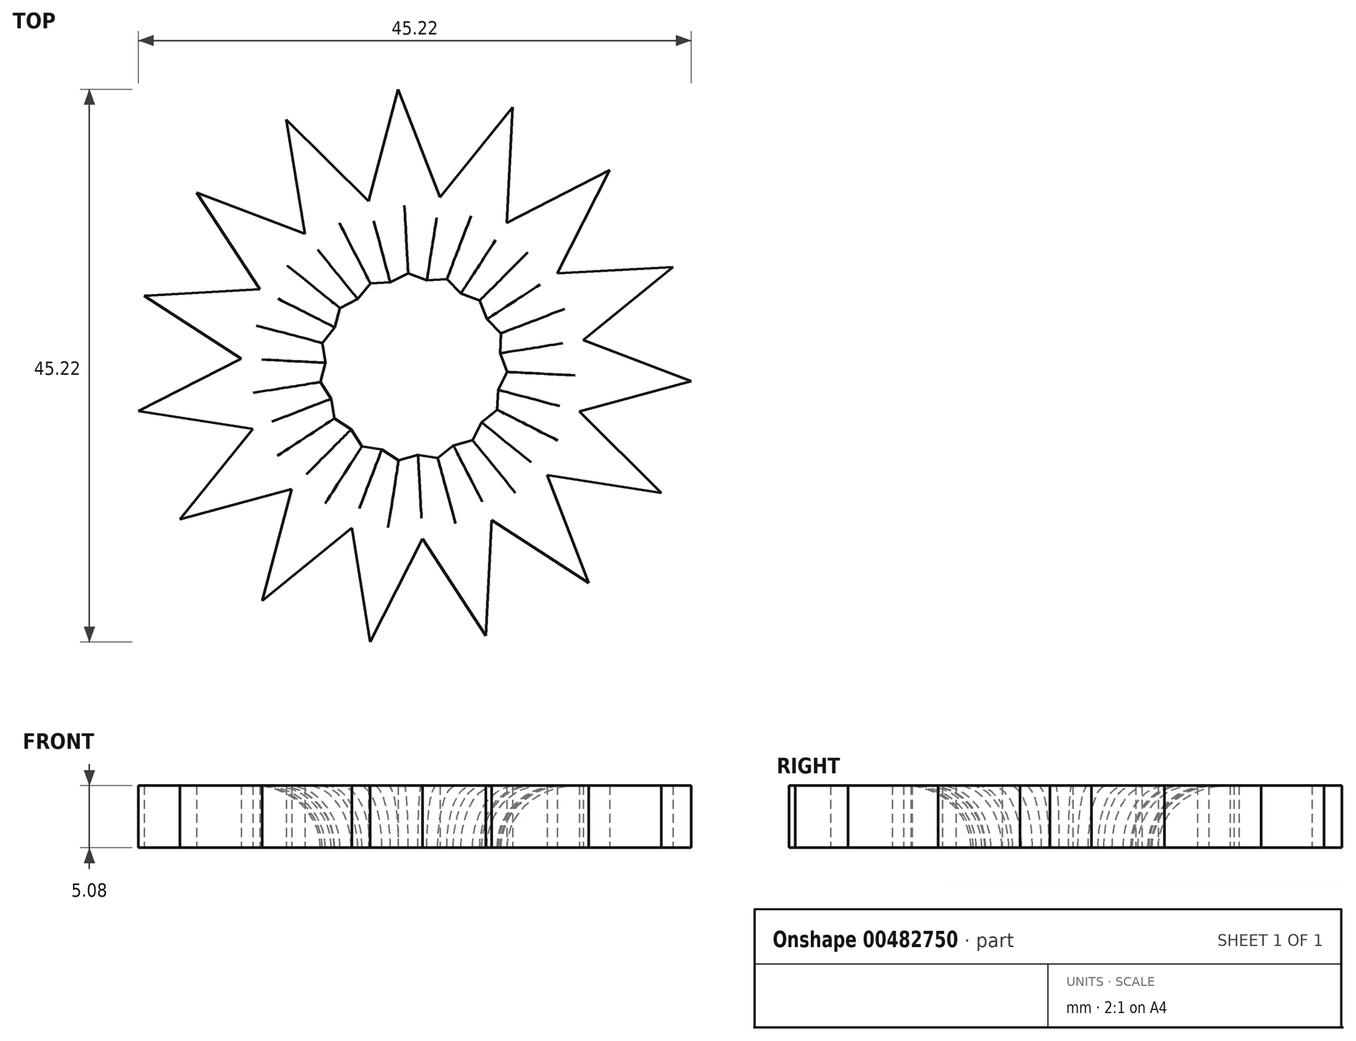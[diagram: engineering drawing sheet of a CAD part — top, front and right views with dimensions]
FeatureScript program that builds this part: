
annotation { "Feature Type Name" : "Feature", "Feature Type Description" : "" }
export const myFeature = defineFeature(function(context is Context, id is Id, definition is map)
    precondition{}
    {
        {
            var Q0;
            Q0=qCreatedBy(makeId("Top.planeOp"),FACE);
            var sketch = newSketch(context, id + "F0", { "sketchPlane" : qUnion([Q0])});
            skLineSegment(sketch, "E0", {"start": v(-12.36, -19.11) * mm, "end": v(-1.23, 22.73) * mm});
            skLineSegment(sketch, "E1", {"start": v(-1.23, 22.73) * mm, "end": v(14.36, -17.67) * mm});
            skLineSegment(sketch, "E2", {"start": v(14.36, -17.67) * mm, "end": v(-22, 5.85) * mm});
            skLineSegment(sketch, "E3", {"start": v(-22, 5.85) * mm, "end": v(21.24, 8.2) * mm});
            skLineSegment(sketch, "E4", {"start": v(21.24, 8.2) * mm, "end": v(-12.36, -19.11) * mm});
            skLineSegment(sketch, "E5", {"start": v(-19.07, -12.43) * mm, "end": v(8.12, 21.27) * mm});
            skLineSegment(sketch, "E6", {"start": v(8.12, 21.27) * mm, "end": v(5.93, -21.98) * mm});
            skLineSegment(sketch, "E7", {"start": v(5.93, -21.98) * mm, "end": v(-17.72, 14.3) * mm});
            skLineSegment(sketch, "E8", {"start": v(-17.72, 14.3) * mm, "end": v(22.74, -1.15) * mm});
            skLineSegment(sketch, "E9", {"start": v(22.74, -1.15) * mm, "end": v(-19.07, -12.43) * mm});
            skLineSegment(sketch, "E10", {"start": v(-3.52, -22.5) * mm, "end": v(-10.37, 20.26) * mm});
            skLineSegment(sketch, "E11", {"start": v(-10.37, 20.26) * mm, "end": v(20.3, -10.3) * mm});
            skLineSegment(sketch, "E12", {"start": v(20.3, -10.3) * mm, "end": v(-22.48, -3.6) * mm});
            skLineSegment(sketch, "E13", {"start": v(-22.48, -3.6) * mm, "end": v(16.07, 16.13) * mm});
            skLineSegment(sketch, "E14", {"start": v(16.07, 16.13) * mm, "end": v(-3.52, -22.5) * mm});
            skSolve(sketch);
        }
        {
            var Q0;
            {var subQ0=sQuery(id+"F0.wireOp",EDGE,"E3");var subQ1=sQuery(id+"F0.wireOp",EDGE,"E2");var subQ2=makeQuery(id+"F0.imprint","INTERSECT",VERTEX,{"derivedFrom":[subQ1,subQ0]});Q0=makeQuery(id+"F0.imprint","IMPRINT",FACE,{"disambiguationData":[TD([[makeQuery(id+"F0.imprint","IMPRINT",EDGE,{"disambiguationData":[TD([[subQ2,1.0]])],"derivedFrom":subQ1}),-1.0]])]});}
            var Q1;
            {var subQ0=sQuery(id+"F0.wireOp",EDGE,"E13");var subQ1=sQuery(id+"F0.wireOp",EDGE,"E2");var subQ2=makeQuery(id+"F0.imprint","INTERSECT",VERTEX,{"derivedFrom":[subQ1,subQ0]});Q1=makeQuery(id+"F0.imprint","IMPRINT",FACE,{"disambiguationData":[TD([[makeQuery(id+"F0.imprint","IMPRINT",EDGE,{"disambiguationData":[TD([[subQ2,1.0]])],"derivedFrom":subQ1}),1.0]])]});}
            var Q2;
            {var subQ0=sQuery(id+"F0.wireOp",EDGE,"E9");var subQ1=sQuery(id+"F0.wireOp",EDGE,"E0");var subQ2=makeQuery(id+"F0.imprint","INTERSECT",VERTEX,{"derivedFrom":[subQ1,subQ0]});Q2=makeQuery(id+"F0.imprint","IMPRINT",FACE,{"disambiguationData":[TD([[makeQuery(id+"F0.imprint","IMPRINT",EDGE,{"disambiguationData":[TD([[subQ2,-1.0]])],"derivedFrom":subQ1}),1.0]])]});}
            var Q3;
            {var subQ0=sQuery(id+"F0.wireOp",EDGE,"E4");var subQ1=sQuery(id+"F0.wireOp",EDGE,"E0");var subQ2=makeQuery(id+"F0.imprint","INTERSECT",VERTEX,{"derivedFrom":[subQ1,subQ0]});Q3=makeQuery(id+"F0.imprint","IMPRINT",FACE,{"disambiguationData":[TD([[makeQuery(id+"F0.imprint","IMPRINT",EDGE,{"disambiguationData":[TD([[subQ2,-1.0]])],"derivedFrom":subQ1}),-1.0]])]});}
            var Q4;
            {var subQ0=sQuery(id+"F0.wireOp",EDGE,"E10");var subQ1=sQuery(id+"F0.wireOp",EDGE,"E4");var subQ2=makeQuery(id+"F0.imprint","INTERSECT",VERTEX,{"derivedFrom":[subQ1,subQ0]});Q4=makeQuery(id+"F0.imprint","IMPRINT",FACE,{"disambiguationData":[TD([[makeQuery(id+"F0.imprint","IMPRINT",EDGE,{"disambiguationData":[TD([[subQ2,1.0]])],"derivedFrom":subQ1}),1.0]])]});}
            var Q5;
            {var subQ0=sQuery(id+"F0.wireOp",EDGE,"E6");var subQ1=sQuery(id+"F0.wireOp",EDGE,"E2");var subQ2=makeQuery(id+"F0.imprint","INTERSECT",VERTEX,{"derivedFrom":[subQ1,subQ0]});Q5=makeQuery(id+"F0.imprint","IMPRINT",FACE,{"disambiguationData":[TD([[makeQuery(id+"F0.imprint","IMPRINT",EDGE,{"disambiguationData":[TD([[subQ2,-1.0]])],"derivedFrom":subQ1}),1.0]])]});}
            var Q6;
            {var subQ0=sQuery(id+"F0.wireOp",EDGE,"E2");var subQ1=sQuery(id+"F0.wireOp",EDGE,"E1");var subQ2=makeQuery(id+"F0.imprint","INTERSECT",VERTEX,{"derivedFrom":[subQ1,subQ0]});Q6=makeQuery(id+"F0.imprint","IMPRINT",FACE,{"disambiguationData":[TD([[makeQuery(id+"F0.imprint","IMPRINT",EDGE,{"disambiguationData":[TD([[subQ2,1.0]])],"derivedFrom":subQ1}),-1.0]])]});}
            var Q7;
            {var subQ0=sQuery(id+"F0.wireOp",EDGE,"E12");var subQ1=sQuery(id+"F0.wireOp",EDGE,"E1");var subQ2=makeQuery(id+"F0.imprint","INTERSECT",VERTEX,{"derivedFrom":[subQ1,subQ0]});Q7=makeQuery(id+"F0.imprint","IMPRINT",FACE,{"disambiguationData":[TD([[makeQuery(id+"F0.imprint","IMPRINT",EDGE,{"disambiguationData":[TD([[subQ2,1.0]])],"derivedFrom":subQ1}),1.0]])]});}
            var Q8;
            {var subQ0=sQuery(id+"F0.wireOp",EDGE,"E8");var subQ1=sQuery(id+"F0.wireOp",EDGE,"E4");var subQ2=makeQuery(id+"F0.imprint","INTERSECT",VERTEX,{"derivedFrom":[subQ1,subQ0]});Q8=makeQuery(id+"F0.imprint","IMPRINT",FACE,{"disambiguationData":[TD([[makeQuery(id+"F0.imprint","IMPRINT",EDGE,{"disambiguationData":[TD([[subQ2,-1.0]])],"derivedFrom":subQ1}),1.0]])]});}
            var Q9;
            {var subQ0=sQuery(id+"F0.wireOp",EDGE,"E4");var subQ1=sQuery(id+"F0.wireOp",EDGE,"E3");var subQ2=makeQuery(id+"F0.imprint","INTERSECT",VERTEX,{"derivedFrom":[subQ1,subQ0]});Q9=makeQuery(id+"F0.imprint","IMPRINT",FACE,{"disambiguationData":[TD([[makeQuery(id+"F0.imprint","IMPRINT",EDGE,{"disambiguationData":[TD([[subQ2,1.0]])],"derivedFrom":subQ1}),-1.0]])]});}
            var Q10;
            {var subQ0=sQuery(id+"F0.wireOp",EDGE,"E14");var subQ1=sQuery(id+"F0.wireOp",EDGE,"E3");var subQ2=makeQuery(id+"F0.imprint","INTERSECT",VERTEX,{"derivedFrom":[subQ1,subQ0]});Q10=makeQuery(id+"F0.imprint","IMPRINT",FACE,{"disambiguationData":[TD([[makeQuery(id+"F0.imprint","IMPRINT",EDGE,{"disambiguationData":[TD([[subQ2,1.0]])],"derivedFrom":subQ1}),1.0]])]});}
            var Q11;
            {var subQ0=sQuery(id+"F0.wireOp",EDGE,"E5");var subQ1=sQuery(id+"F0.wireOp",EDGE,"E1");var subQ2=makeQuery(id+"F0.imprint","INTERSECT",VERTEX,{"derivedFrom":[subQ1,subQ0]});Q11=makeQuery(id+"F0.imprint","IMPRINT",FACE,{"disambiguationData":[TD([[makeQuery(id+"F0.imprint","IMPRINT",EDGE,{"disambiguationData":[TD([[subQ2,-1.0]])],"derivedFrom":subQ1}),1.0]])]});}
            var Q12;
            {var subQ0=sQuery(id+"F0.wireOp",EDGE,"E1");var subQ1=sQuery(id+"F0.wireOp",EDGE,"E0");var subQ2=makeQuery(id+"F0.imprint","INTERSECT",VERTEX,{"derivedFrom":[subQ1,subQ0]});Q12=makeQuery(id+"F0.imprint","IMPRINT",FACE,{"disambiguationData":[TD([[makeQuery(id+"F0.imprint","IMPRINT",EDGE,{"disambiguationData":[TD([[subQ2,1.0]])],"derivedFrom":subQ1}),-1.0]])]});}
            var Q13;
            {var subQ0=sQuery(id+"F0.wireOp",EDGE,"E11");var subQ1=sQuery(id+"F0.wireOp",EDGE,"E0");var subQ2=makeQuery(id+"F0.imprint","INTERSECT",VERTEX,{"derivedFrom":[subQ1,subQ0]});Q13=makeQuery(id+"F0.imprint","IMPRINT",FACE,{"disambiguationData":[TD([[makeQuery(id+"F0.imprint","IMPRINT",EDGE,{"disambiguationData":[TD([[subQ2,1.0]])],"derivedFrom":subQ1}),1.0]])]});}
            var Q14;
            {var subQ0=sQuery(id+"F0.wireOp",EDGE,"E7");var subQ1=sQuery(id+"F0.wireOp",EDGE,"E3");var subQ2=makeQuery(id+"F0.imprint","INTERSECT",VERTEX,{"derivedFrom":[subQ1,subQ0]});Q14=makeQuery(id+"F0.imprint","IMPRINT",FACE,{"disambiguationData":[TD([[makeQuery(id+"F0.imprint","IMPRINT",EDGE,{"disambiguationData":[TD([[subQ2,-1.0]])],"derivedFrom":subQ1}),1.0]])]});}
            var Q15;
            {var subQ0=sQuery(id+"F0.wireOp",EDGE,"E7");var subQ1=sQuery(id+"F0.wireOp",EDGE,"E3");var subQ2=makeQuery(id+"F0.imprint","INTERSECT",VERTEX,{"derivedFrom":[subQ1,subQ0]});Q15=makeQuery(id+"F0.imprint","IMPRINT",FACE,{"disambiguationData":[TD([[makeQuery(id+"F0.imprint","IMPRINT",EDGE,{"disambiguationData":[TD([[subQ2,-1.0]])],"derivedFrom":subQ1}),-1.0]])]});}
            var Q16;
            {var subQ0=sQuery(id+"F0.wireOp",EDGE,"E13");var subQ1=sQuery(id+"F0.wireOp",EDGE,"E2");var subQ2=makeQuery(id+"F0.imprint","INTERSECT",VERTEX,{"derivedFrom":[subQ1,subQ0]});Q16=makeQuery(id+"F0.imprint","IMPRINT",FACE,{"disambiguationData":[TD([[makeQuery(id+"F0.imprint","IMPRINT",EDGE,{"disambiguationData":[TD([[subQ2,1.0]])],"derivedFrom":subQ1}),-1.0]])]});}
            var Q17;
            {var subQ0=sQuery(id+"F0.wireOp",EDGE,"E12");var subQ1=sQuery(id+"F0.wireOp",EDGE,"E0");var subQ2=makeQuery(id+"F0.imprint","INTERSECT",VERTEX,{"derivedFrom":[subQ1,subQ0]});Q17=makeQuery(id+"F0.imprint","IMPRINT",FACE,{"disambiguationData":[TD([[makeQuery(id+"F0.imprint","IMPRINT",EDGE,{"disambiguationData":[TD([[subQ2,-1.0]])],"derivedFrom":subQ1}),1.0]])]});}
            var Q18;
            {var subQ0=sQuery(id+"F0.wireOp",EDGE,"E9");var subQ1=sQuery(id+"F0.wireOp",EDGE,"E0");var subQ2=makeQuery(id+"F0.imprint","INTERSECT",VERTEX,{"derivedFrom":[subQ1,subQ0]});Q18=makeQuery(id+"F0.imprint","IMPRINT",FACE,{"disambiguationData":[TD([[makeQuery(id+"F0.imprint","IMPRINT",EDGE,{"disambiguationData":[TD([[subQ2,-1.0]])],"derivedFrom":subQ1}),-1.0]])]});}
            var Q19;
            {var subQ0=sQuery(id+"F0.wireOp",EDGE,"E10");var subQ1=sQuery(id+"F0.wireOp",EDGE,"E4");var subQ2=makeQuery(id+"F0.imprint","INTERSECT",VERTEX,{"derivedFrom":[subQ1,subQ0]});Q19=makeQuery(id+"F0.imprint","IMPRINT",FACE,{"disambiguationData":[TD([[makeQuery(id+"F0.imprint","IMPRINT",EDGE,{"disambiguationData":[TD([[subQ2,1.0]])],"derivedFrom":subQ1}),-1.0]])]});}
            var Q20;
            {var subQ0=sQuery(id+"F0.wireOp",EDGE,"E14");var subQ1=sQuery(id+"F0.wireOp",EDGE,"E2");var subQ2=makeQuery(id+"F0.imprint","INTERSECT",VERTEX,{"derivedFrom":[subQ1,subQ0]});Q20=makeQuery(id+"F0.imprint","IMPRINT",FACE,{"disambiguationData":[TD([[makeQuery(id+"F0.imprint","IMPRINT",EDGE,{"disambiguationData":[TD([[subQ2,-1.0]])],"derivedFrom":subQ1}),1.0]])]});}
            var Q21;
            {var subQ0=sQuery(id+"F0.wireOp",EDGE,"E6");var subQ1=sQuery(id+"F0.wireOp",EDGE,"E2");var subQ2=makeQuery(id+"F0.imprint","INTERSECT",VERTEX,{"derivedFrom":[subQ1,subQ0]});Q21=makeQuery(id+"F0.imprint","IMPRINT",FACE,{"disambiguationData":[TD([[makeQuery(id+"F0.imprint","IMPRINT",EDGE,{"disambiguationData":[TD([[subQ2,-1.0]])],"derivedFrom":subQ1}),-1.0]])]});}
            var Q22;
            {var subQ0=sQuery(id+"F0.wireOp",EDGE,"E12");var subQ1=sQuery(id+"F0.wireOp",EDGE,"E1");var subQ2=makeQuery(id+"F0.imprint","INTERSECT",VERTEX,{"derivedFrom":[subQ1,subQ0]});Q22=makeQuery(id+"F0.imprint","IMPRINT",FACE,{"disambiguationData":[TD([[makeQuery(id+"F0.imprint","IMPRINT",EDGE,{"disambiguationData":[TD([[subQ2,1.0]])],"derivedFrom":subQ1}),-1.0]])]});}
            var Q23;
            {var subQ0=sQuery(id+"F0.wireOp",EDGE,"E4");var subQ1=sQuery(id+"F0.wireOp",EDGE,"E1");var subQ2=makeQuery(id+"F0.imprint","INTERSECT",VERTEX,{"derivedFrom":[subQ1,subQ0]});Q23=makeQuery(id+"F0.imprint","IMPRINT",FACE,{"disambiguationData":[TD([[makeQuery(id+"F0.imprint","IMPRINT",EDGE,{"disambiguationData":[TD([[subQ2,-1.0]])],"derivedFrom":subQ1}),1.0]])]});}
            var Q24;
            {var subQ0=sQuery(id+"F0.wireOp",EDGE,"E8");var subQ1=sQuery(id+"F0.wireOp",EDGE,"E4");var subQ2=makeQuery(id+"F0.imprint","INTERSECT",VERTEX,{"derivedFrom":[subQ1,subQ0]});Q24=makeQuery(id+"F0.imprint","IMPRINT",FACE,{"disambiguationData":[TD([[makeQuery(id+"F0.imprint","IMPRINT",EDGE,{"disambiguationData":[TD([[subQ2,-1.0]])],"derivedFrom":subQ1}),-1.0]])]});}
            var Q25;
            {var subQ0=sQuery(id+"F0.wireOp",EDGE,"E14");var subQ1=sQuery(id+"F0.wireOp",EDGE,"E3");var subQ2=makeQuery(id+"F0.imprint","INTERSECT",VERTEX,{"derivedFrom":[subQ1,subQ0]});Q25=makeQuery(id+"F0.imprint","IMPRINT",FACE,{"disambiguationData":[TD([[makeQuery(id+"F0.imprint","IMPRINT",EDGE,{"disambiguationData":[TD([[subQ2,1.0]])],"derivedFrom":subQ1}),-1.0]])]});}
            var Q26;
            {var subQ0=sQuery(id+"F0.wireOp",EDGE,"E13");var subQ1=sQuery(id+"F0.wireOp",EDGE,"E1");var subQ2=makeQuery(id+"F0.imprint","INTERSECT",VERTEX,{"derivedFrom":[subQ1,subQ0]});Q26=makeQuery(id+"F0.imprint","IMPRINT",FACE,{"disambiguationData":[TD([[makeQuery(id+"F0.imprint","IMPRINT",EDGE,{"disambiguationData":[TD([[subQ2,-1.0]])],"derivedFrom":subQ1}),1.0]])]});}
            var Q27;
            {var subQ0=sQuery(id+"F0.wireOp",EDGE,"E5");var subQ1=sQuery(id+"F0.wireOp",EDGE,"E1");var subQ2=makeQuery(id+"F0.imprint","INTERSECT",VERTEX,{"derivedFrom":[subQ1,subQ0]});Q27=makeQuery(id+"F0.imprint","IMPRINT",FACE,{"disambiguationData":[TD([[makeQuery(id+"F0.imprint","IMPRINT",EDGE,{"disambiguationData":[TD([[subQ2,-1.0]])],"derivedFrom":subQ1}),-1.0]])]});}
            var Q28;
            {var subQ0=sQuery(id+"F0.wireOp",EDGE,"E11");var subQ1=sQuery(id+"F0.wireOp",EDGE,"E0");var subQ2=makeQuery(id+"F0.imprint","INTERSECT",VERTEX,{"derivedFrom":[subQ1,subQ0]});Q28=makeQuery(id+"F0.imprint","IMPRINT",FACE,{"disambiguationData":[TD([[makeQuery(id+"F0.imprint","IMPRINT",EDGE,{"disambiguationData":[TD([[subQ2,1.0]])],"derivedFrom":subQ1}),-1.0]])]});}
            var Q29;
            {var subQ0=sQuery(id+"F0.wireOp",EDGE,"E3");var subQ1=sQuery(id+"F0.wireOp",EDGE,"E0");var subQ2=makeQuery(id+"F0.imprint","INTERSECT",VERTEX,{"derivedFrom":[subQ1,subQ0]});Q29=makeQuery(id+"F0.imprint","IMPRINT",FACE,{"disambiguationData":[TD([[makeQuery(id+"F0.imprint","IMPRINT",EDGE,{"disambiguationData":[TD([[subQ2,-1.0]])],"derivedFrom":subQ1}),1.0]])]});}
            var Q30;
            {var subQ0=sQuery(id+"F0.wireOp",EDGE,"E7");var subQ1=sQuery(id+"F0.wireOp",EDGE,"E5");var subQ2=makeQuery(id+"F0.imprint","INTERSECT",VERTEX,{"derivedFrom":[subQ1,subQ0]});Q30=makeQuery(id+"F0.imprint","IMPRINT",FACE,{"disambiguationData":[TD([[makeQuery(id+"F0.imprint","IMPRINT",EDGE,{"disambiguationData":[TD([[subQ2,-1.0]])],"derivedFrom":subQ1}),1.0]])]});}
            var Q31;
            {var subQ0=sQuery(id+"F0.wireOp",EDGE,"E2");var subQ1=sQuery(id+"F0.wireOp",EDGE,"E0");var subQ2=makeQuery(id+"F0.imprint","INTERSECT",VERTEX,{"derivedFrom":[subQ1,subQ0]});Q31=makeQuery(id+"F0.imprint","IMPRINT",FACE,{"disambiguationData":[TD([[makeQuery(id+"F0.imprint","IMPRINT",EDGE,{"disambiguationData":[TD([[subQ2,-1.0]])],"derivedFrom":subQ1}),1.0]])]});}
            var Q32;
            {var subQ0=sQuery(id+"F0.wireOp",EDGE,"E12");var subQ1=sQuery(id+"F0.wireOp",EDGE,"E0");var subQ2=makeQuery(id+"F0.imprint","INTERSECT",VERTEX,{"derivedFrom":[subQ1,subQ0]});Q32=makeQuery(id+"F0.imprint","IMPRINT",FACE,{"disambiguationData":[TD([[makeQuery(id+"F0.imprint","IMPRINT",EDGE,{"disambiguationData":[TD([[subQ2,-1.0]])],"derivedFrom":subQ1}),-1.0]])]});}
            var Q33;
            {var subQ0=sQuery(id+"F0.wireOp",EDGE,"E9");var subQ1=sQuery(id+"F0.wireOp",EDGE,"E7");var subQ2=makeQuery(id+"F0.imprint","INTERSECT",VERTEX,{"derivedFrom":[subQ1,subQ0]});Q33=makeQuery(id+"F0.imprint","IMPRINT",FACE,{"disambiguationData":[TD([[makeQuery(id+"F0.imprint","IMPRINT",EDGE,{"disambiguationData":[TD([[subQ2,-1.0]])],"derivedFrom":subQ1}),1.0]])]});}
            var Q34;
            {var subQ0=sQuery(id+"F0.wireOp",EDGE,"E4");var subQ1=sQuery(id+"F0.wireOp",EDGE,"E2");var subQ2=makeQuery(id+"F0.imprint","INTERSECT",VERTEX,{"derivedFrom":[subQ1,subQ0]});Q34=makeQuery(id+"F0.imprint","IMPRINT",FACE,{"disambiguationData":[TD([[makeQuery(id+"F0.imprint","IMPRINT",EDGE,{"disambiguationData":[TD([[subQ2,-1.0]])],"derivedFrom":subQ1}),1.0]])]});}
            var Q35;
            {var subQ0=sQuery(id+"F0.wireOp",EDGE,"E14");var subQ1=sQuery(id+"F0.wireOp",EDGE,"E2");var subQ2=makeQuery(id+"F0.imprint","INTERSECT",VERTEX,{"derivedFrom":[subQ1,subQ0]});Q35=makeQuery(id+"F0.imprint","IMPRINT",FACE,{"disambiguationData":[TD([[makeQuery(id+"F0.imprint","IMPRINT",EDGE,{"disambiguationData":[TD([[subQ2,-1.0]])],"derivedFrom":subQ1}),-1.0]])]});}
            var Q36;
            {var subQ0=sQuery(id+"F0.wireOp",EDGE,"E9");var subQ1=sQuery(id+"F0.wireOp",EDGE,"E6");var subQ2=makeQuery(id+"F0.imprint","INTERSECT",VERTEX,{"derivedFrom":[subQ1,subQ0]});Q36=makeQuery(id+"F0.imprint","IMPRINT",FACE,{"disambiguationData":[TD([[makeQuery(id+"F0.imprint","IMPRINT",EDGE,{"disambiguationData":[TD([[subQ2,-1.0]])],"derivedFrom":subQ1}),-1.0]])]});}
            var Q37;
            {var subQ0=sQuery(id+"F0.wireOp",EDGE,"E4");var subQ1=sQuery(id+"F0.wireOp",EDGE,"E1");var subQ2=makeQuery(id+"F0.imprint","INTERSECT",VERTEX,{"derivedFrom":[subQ1,subQ0]});Q37=makeQuery(id+"F0.imprint","IMPRINT",FACE,{"disambiguationData":[TD([[makeQuery(id+"F0.imprint","IMPRINT",EDGE,{"disambiguationData":[TD([[subQ2,-1.0]])],"derivedFrom":subQ1}),-1.0]])]});}
            var Q38;
            {var subQ0=sQuery(id+"F0.wireOp",EDGE,"E14");var subQ1=sQuery(id+"F0.wireOp",EDGE,"E1");var subQ2=makeQuery(id+"F0.imprint","INTERSECT",VERTEX,{"derivedFrom":[subQ1,subQ0]});Q38=makeQuery(id+"F0.imprint","IMPRINT",FACE,{"disambiguationData":[TD([[makeQuery(id+"F0.imprint","IMPRINT",EDGE,{"disambiguationData":[TD([[subQ2,-1.0]])],"derivedFrom":subQ1}),1.0]])]});}
            var Q39;
            {var subQ0=sQuery(id+"F0.wireOp",EDGE,"E8");var subQ1=sQuery(id+"F0.wireOp",EDGE,"E6");var subQ2=makeQuery(id+"F0.imprint","INTERSECT",VERTEX,{"derivedFrom":[subQ1,subQ0]});Q39=makeQuery(id+"F0.imprint","IMPRINT",FACE,{"disambiguationData":[TD([[makeQuery(id+"F0.imprint","IMPRINT",EDGE,{"disambiguationData":[TD([[subQ2,-1.0]])],"derivedFrom":subQ1}),1.0]])]});}
            var Q40;
            {var subQ0=sQuery(id+"F0.wireOp",EDGE,"E3");var subQ1=sQuery(id+"F0.wireOp",EDGE,"E1");var subQ2=makeQuery(id+"F0.imprint","INTERSECT",VERTEX,{"derivedFrom":[subQ1,subQ0]});Q40=makeQuery(id+"F0.imprint","IMPRINT",FACE,{"disambiguationData":[TD([[makeQuery(id+"F0.imprint","IMPRINT",EDGE,{"disambiguationData":[TD([[subQ2,-1.0]])],"derivedFrom":subQ1}),1.0]])]});}
            var Q41;
            {var subQ0=sQuery(id+"F0.wireOp",EDGE,"E8");var subQ1=sQuery(id+"F0.wireOp",EDGE,"E5");var subQ2=makeQuery(id+"F0.imprint","INTERSECT",VERTEX,{"derivedFrom":[subQ1,subQ0]});Q41=makeQuery(id+"F0.imprint","IMPRINT",FACE,{"disambiguationData":[TD([[makeQuery(id+"F0.imprint","IMPRINT",EDGE,{"disambiguationData":[TD([[subQ2,-1.0]])],"derivedFrom":subQ1}),-1.0]])]});}
            var Q42;
            {var subQ0=sQuery(id+"F0.wireOp",EDGE,"E3");var subQ1=sQuery(id+"F0.wireOp",EDGE,"E0");var subQ2=makeQuery(id+"F0.imprint","INTERSECT",VERTEX,{"derivedFrom":[subQ1,subQ0]});Q42=makeQuery(id+"F0.imprint","IMPRINT",FACE,{"disambiguationData":[TD([[makeQuery(id+"F0.imprint","IMPRINT",EDGE,{"disambiguationData":[TD([[subQ2,-1.0]])],"derivedFrom":subQ1}),-1.0]])]});}
            var Q43;
            {var subQ0=sQuery(id+"F0.wireOp",EDGE,"E5");var subQ1=sQuery(id+"F0.wireOp",EDGE,"E0");var subQ2=makeQuery(id+"F0.imprint","INTERSECT",VERTEX,{"derivedFrom":[subQ1,subQ0]});Q43=makeQuery(id+"F0.imprint","IMPRINT",FACE,{"disambiguationData":[TD([[makeQuery(id+"F0.imprint","IMPRINT",EDGE,{"disambiguationData":[TD([[subQ2,-1.0]])],"derivedFrom":subQ1}),1.0]])]});}
            var Q44;
            {var subQ0=sQuery(id+"F0.wireOp",EDGE,"E7");var subQ1=sQuery(id+"F0.wireOp",EDGE,"E0");var subQ2=makeQuery(id+"F0.imprint","INTERSECT",VERTEX,{"derivedFrom":[subQ1,subQ0]});Q44=makeQuery(id+"F0.imprint","IMPRINT",FACE,{"disambiguationData":[TD([[makeQuery(id+"F0.imprint","IMPRINT",EDGE,{"disambiguationData":[TD([[subQ2,-1.0]])],"derivedFrom":subQ1}),1.0]])]});}
            var Q45;
            {var subQ0=sQuery(id+"F0.wireOp",EDGE,"E2");var subQ1=sQuery(id+"F0.wireOp",EDGE,"E0");var subQ2=makeQuery(id+"F0.imprint","INTERSECT",VERTEX,{"derivedFrom":[subQ1,subQ0]});Q45=makeQuery(id+"F0.imprint","IMPRINT",FACE,{"disambiguationData":[TD([[makeQuery(id+"F0.imprint","IMPRINT",EDGE,{"disambiguationData":[TD([[subQ2,-1.0]])],"derivedFrom":subQ1}),-1.0]])]});}
            var Q46;
            {var subQ0=sQuery(id+"F0.wireOp",EDGE,"E7");var subQ1=sQuery(id+"F0.wireOp",EDGE,"E2");var subQ2=makeQuery(id+"F0.imprint","INTERSECT",VERTEX,{"derivedFrom":[subQ1,subQ0]});Q46=makeQuery(id+"F0.imprint","IMPRINT",FACE,{"disambiguationData":[TD([[makeQuery(id+"F0.imprint","IMPRINT",EDGE,{"disambiguationData":[TD([[subQ2,-1.0]])],"derivedFrom":subQ1}),1.0]])]});}
            var Q47;
            {var subQ0=sQuery(id+"F0.wireOp",EDGE,"E9");var subQ1=sQuery(id+"F0.wireOp",EDGE,"E2");var subQ2=makeQuery(id+"F0.imprint","INTERSECT",VERTEX,{"derivedFrom":[subQ1,subQ0]});Q47=makeQuery(id+"F0.imprint","IMPRINT",FACE,{"disambiguationData":[TD([[makeQuery(id+"F0.imprint","IMPRINT",EDGE,{"disambiguationData":[TD([[subQ2,-1.0]])],"derivedFrom":subQ1}),1.0]])]});}
            var Q48;
            {var subQ0=sQuery(id+"F0.wireOp",EDGE,"E4");var subQ1=sQuery(id+"F0.wireOp",EDGE,"E2");var subQ2=makeQuery(id+"F0.imprint","INTERSECT",VERTEX,{"derivedFrom":[subQ1,subQ0]});Q48=makeQuery(id+"F0.imprint","IMPRINT",FACE,{"disambiguationData":[TD([[makeQuery(id+"F0.imprint","IMPRINT",EDGE,{"disambiguationData":[TD([[subQ2,-1.0]])],"derivedFrom":subQ1}),-1.0]])]});}
            var Q49;
            {var subQ0=sQuery(id+"F0.wireOp",EDGE,"E9");var subQ1=sQuery(id+"F0.wireOp",EDGE,"E4");var subQ2=makeQuery(id+"F0.imprint","INTERSECT",VERTEX,{"derivedFrom":[subQ1,subQ0]});Q49=makeQuery(id+"F0.imprint","IMPRINT",FACE,{"disambiguationData":[TD([[makeQuery(id+"F0.imprint","IMPRINT",EDGE,{"disambiguationData":[TD([[subQ2,-1.0]])],"derivedFrom":subQ1}),1.0]])]});}
            var Q50;
            {var subQ0=sQuery(id+"F0.wireOp",EDGE,"E6");var subQ1=sQuery(id+"F0.wireOp",EDGE,"E4");var subQ2=makeQuery(id+"F0.imprint","INTERSECT",VERTEX,{"derivedFrom":[subQ1,subQ0]});Q50=makeQuery(id+"F0.imprint","IMPRINT",FACE,{"disambiguationData":[TD([[makeQuery(id+"F0.imprint","IMPRINT",EDGE,{"disambiguationData":[TD([[subQ2,-1.0]])],"derivedFrom":subQ1}),1.0]])]});}
            var Q51;
            {var subQ0=sQuery(id+"F0.wireOp",EDGE,"E14");var subQ1=sQuery(id+"F0.wireOp",EDGE,"E1");var subQ2=makeQuery(id+"F0.imprint","INTERSECT",VERTEX,{"derivedFrom":[subQ1,subQ0]});Q51=makeQuery(id+"F0.imprint","IMPRINT",FACE,{"disambiguationData":[TD([[makeQuery(id+"F0.imprint","IMPRINT",EDGE,{"disambiguationData":[TD([[subQ2,-1.0]])],"derivedFrom":subQ1}),-1.0]])]});}
            var Q52;
            {var subQ0=sQuery(id+"F0.wireOp",EDGE,"E6");var subQ1=sQuery(id+"F0.wireOp",EDGE,"E1");var subQ2=makeQuery(id+"F0.imprint","INTERSECT",VERTEX,{"derivedFrom":[subQ1,subQ0]});Q52=makeQuery(id+"F0.imprint","IMPRINT",FACE,{"disambiguationData":[TD([[makeQuery(id+"F0.imprint","IMPRINT",EDGE,{"disambiguationData":[TD([[subQ2,-1.0]])],"derivedFrom":subQ1}),1.0]])]});}
            var Q53;
            {var subQ0=sQuery(id+"F0.wireOp",EDGE,"E13");var subQ1=sQuery(id+"F0.wireOp",EDGE,"E1");var subQ2=makeQuery(id+"F0.imprint","INTERSECT",VERTEX,{"derivedFrom":[subQ1,subQ0]});Q53=makeQuery(id+"F0.imprint","IMPRINT",FACE,{"disambiguationData":[TD([[makeQuery(id+"F0.imprint","IMPRINT",EDGE,{"disambiguationData":[TD([[subQ2,-1.0]])],"derivedFrom":subQ1}),-1.0]])]});}
            var Q54;
            {var subQ0=sQuery(id+"F0.wireOp",EDGE,"E3");var subQ1=sQuery(id+"F0.wireOp",EDGE,"E1");var subQ2=makeQuery(id+"F0.imprint","INTERSECT",VERTEX,{"derivedFrom":[subQ1,subQ0]});Q54=makeQuery(id+"F0.imprint","IMPRINT",FACE,{"disambiguationData":[TD([[makeQuery(id+"F0.imprint","IMPRINT",EDGE,{"disambiguationData":[TD([[subQ2,-1.0]])],"derivedFrom":subQ1}),-1.0]])]});}
            var Q55;
            {var subQ0=sQuery(id+"F0.wireOp",EDGE,"E8");var subQ1=sQuery(id+"F0.wireOp",EDGE,"E3");var subQ2=makeQuery(id+"F0.imprint","INTERSECT",VERTEX,{"derivedFrom":[subQ1,subQ0]});Q55=makeQuery(id+"F0.imprint","IMPRINT",FACE,{"disambiguationData":[TD([[makeQuery(id+"F0.imprint","IMPRINT",EDGE,{"disambiguationData":[TD([[subQ2,-1.0]])],"derivedFrom":subQ1}),1.0]])]});}
            var Q56;
            {var subQ0=sQuery(id+"F0.wireOp",EDGE,"E5");var subQ1=sQuery(id+"F0.wireOp",EDGE,"E3");var subQ2=makeQuery(id+"F0.imprint","INTERSECT",VERTEX,{"derivedFrom":[subQ1,subQ0]});Q56=makeQuery(id+"F0.imprint","IMPRINT",FACE,{"disambiguationData":[TD([[makeQuery(id+"F0.imprint","IMPRINT",EDGE,{"disambiguationData":[TD([[subQ2,-1.0]])],"derivedFrom":subQ1}),1.0]])]});}
            var Q57;
            {var subQ0=sQuery(id+"F0.wireOp",EDGE,"E13");var subQ1=sQuery(id+"F0.wireOp",EDGE,"E0");var subQ2=makeQuery(id+"F0.imprint","INTERSECT",VERTEX,{"derivedFrom":[subQ1,subQ0]});Q57=makeQuery(id+"F0.imprint","IMPRINT",FACE,{"disambiguationData":[TD([[makeQuery(id+"F0.imprint","IMPRINT",EDGE,{"disambiguationData":[TD([[subQ2,-1.0]])],"derivedFrom":subQ1}),-1.0]])]});}
            var Q58;
            {var subQ0=sQuery(id+"F0.wireOp",EDGE,"E13");var subQ1=sQuery(id+"F0.wireOp",EDGE,"E0");var subQ2=makeQuery(id+"F0.imprint","INTERSECT",VERTEX,{"derivedFrom":[subQ1,subQ0]});Q58=makeQuery(id+"F0.imprint","IMPRINT",FACE,{"disambiguationData":[TD([[makeQuery(id+"F0.imprint","IMPRINT",EDGE,{"disambiguationData":[TD([[subQ2,-1.0]])],"derivedFrom":subQ1}),1.0]])]});}
            var Q59;
            {var subQ0=sQuery(id+"F0.wireOp",EDGE,"E8");var subQ1=sQuery(id+"F0.wireOp",EDGE,"E1");var subQ2=makeQuery(id+"F0.imprint","INTERSECT",VERTEX,{"derivedFrom":[subQ1,subQ0]});Q59=makeQuery(id+"F0.imprint","IMPRINT",FACE,{"disambiguationData":[TD([[makeQuery(id+"F0.imprint","IMPRINT",EDGE,{"disambiguationData":[TD([[subQ2,-1.0]])],"derivedFrom":subQ1}),1.0]])]});}
            extrude(context, id + "F1", {"entities" : qUnion([Q0, Q1, Q2, Q3, Q4, Q5, Q6, Q7, Q8, Q9, Q10, Q11, Q12, Q13, Q14, Q15, Q16, Q17, Q18, Q19, Q20, Q21, Q22, Q23, Q24, Q25, Q26, Q27, Q28, Q29, Q30, Q31, Q32, Q33, Q34, Q35, Q36, Q37, Q38, Q39, Q40, Q41, Q42, Q43, Q44, Q45, Q46, Q47, Q48, Q49, Q50, Q51, Q52, Q53, Q54, Q55, Q56, Q57, Q58, Q59]), "depth" : 5.08 * mm});
        }
        {
            var Q0;
            {var subQ0=sQuery(id+"F0.wireOp",EDGE,"E0");Q0=makeQuery(id+"F1.opExtrude","CAP_EDGE",EDGE,{"disambiguationData":[OSD([subQ0]),TDD([makeQuery(id+"F0.imprint","IMPRINT",EDGE,{"disambiguationData":[TD([[makeQuery(id+"F0.imprint","INTERSECT",VERTEX,{"derivedFrom":[subQ0,sQuery(id+"F0.wireOp",EDGE,"E5")]}),-1.0]])],"derivedFrom":subQ0})])],"isStart":false});}
            var Q1;
            {var subQ0=sQuery(id+"F0.wireOp",EDGE,"E5");Q1=makeQuery(id+"F1.opExtrude","CAP_EDGE",EDGE,{"disambiguationData":[OSD([subQ0]),TDD([makeQuery(id+"F0.imprint","IMPRINT",EDGE,{"disambiguationData":[TD([[makeQuery(id+"F0.imprint","INTERSECT",VERTEX,{"derivedFrom":[sQuery(id+"F0.wireOp",EDGE,"E0"),subQ0]}),1.0]])],"derivedFrom":subQ0})])],"isStart":false});}
            var Q2;
            {var subQ0=sQuery(id+"F0.wireOp",EDGE,"E10");Q2=makeQuery(id+"F1.opExtrude","CAP_EDGE",EDGE,{"disambiguationData":[OSD([subQ0]),TDD([makeQuery(id+"F0.imprint","IMPRINT",EDGE,{"disambiguationData":[TD([[makeQuery(id+"F0.imprint","INTERSECT",VERTEX,{"derivedFrom":[sQuery(id+"F0.wireOp",EDGE,"E0"),subQ0]}),-1.0]])],"derivedFrom":subQ0})])],"isStart":false});}
            var Q3;
            {var subQ0=sQuery(id+"F0.wireOp",EDGE,"E0");Q3=makeQuery(id+"F1.opExtrude","CAP_EDGE",EDGE,{"disambiguationData":[OSD([subQ0]),TDD([makeQuery(id+"F0.imprint","IMPRINT",EDGE,{"disambiguationData":[TD([[makeQuery(id+"F0.imprint","INTERSECT",VERTEX,{"derivedFrom":[subQ0,sQuery(id+"F0.wireOp",EDGE,"E7")]}),-1.0]])],"derivedFrom":subQ0})])],"isStart":false});}
            var Q4;
            {var subQ0=sQuery(id+"F0.wireOp",EDGE,"E7");Q4=makeQuery(id+"F1.opExtrude","CAP_EDGE",EDGE,{"disambiguationData":[OSD([subQ0]),TDD([makeQuery(id+"F0.imprint","IMPRINT",EDGE,{"disambiguationData":[TD([[makeQuery(id+"F0.imprint","INTERSECT",VERTEX,{"derivedFrom":[sQuery(id+"F0.wireOp",EDGE,"E0"),subQ0]}),1.0]])],"derivedFrom":subQ0})])],"isStart":false});}
            var Q5;
            {var subQ0=sQuery(id+"F0.wireOp",EDGE,"E10");Q5=makeQuery(id+"F1.opExtrude","CAP_EDGE",EDGE,{"disambiguationData":[OSD([subQ0]),TDD([makeQuery(id+"F0.imprint","IMPRINT",EDGE,{"disambiguationData":[TD([[makeQuery(id+"F0.imprint","INTERSECT",VERTEX,{"derivedFrom":[sQuery(id+"F0.wireOp",EDGE,"E2"),subQ0]}),-1.0]])],"derivedFrom":subQ0})])],"isStart":false});}
            var Q6;
            {var subQ0=sQuery(id+"F0.wireOp",EDGE,"E2");Q6=makeQuery(id+"F1.opExtrude","CAP_EDGE",EDGE,{"disambiguationData":[OSD([subQ0]),TDD([makeQuery(id+"F0.imprint","IMPRINT",EDGE,{"disambiguationData":[TD([[makeQuery(id+"F0.imprint","INTERSECT",VERTEX,{"derivedFrom":[subQ0,sQuery(id+"F0.wireOp",EDGE,"E7")]}),-1.0]])],"derivedFrom":subQ0})])],"isStart":false});}
            var Q7;
            {var subQ0=sQuery(id+"F0.wireOp",EDGE,"E7");Q7=makeQuery(id+"F1.opExtrude","CAP_EDGE",EDGE,{"disambiguationData":[OSD([subQ0]),TDD([makeQuery(id+"F0.imprint","IMPRINT",EDGE,{"disambiguationData":[TD([[makeQuery(id+"F0.imprint","INTERSECT",VERTEX,{"derivedFrom":[sQuery(id+"F0.wireOp",EDGE,"E2"),subQ0]}),1.0]])],"derivedFrom":subQ0})])],"isStart":false});}
            var Q8;
            {var subQ0=sQuery(id+"F0.wireOp",EDGE,"E12");Q8=makeQuery(id+"F1.opExtrude","CAP_EDGE",EDGE,{"disambiguationData":[OSD([subQ0]),TDD([makeQuery(id+"F0.imprint","IMPRINT",EDGE,{"disambiguationData":[TD([[makeQuery(id+"F0.imprint","INTERSECT",VERTEX,{"derivedFrom":[sQuery(id+"F0.wireOp",EDGE,"E2"),subQ0]}),-1.0]])],"derivedFrom":subQ0})])],"isStart":false});}
            var Q9;
            {var subQ0=sQuery(id+"F0.wireOp",EDGE,"E2");Q9=makeQuery(id+"F1.opExtrude","CAP_EDGE",EDGE,{"disambiguationData":[OSD([subQ0]),TDD([makeQuery(id+"F0.imprint","IMPRINT",EDGE,{"disambiguationData":[TD([[makeQuery(id+"F0.imprint","INTERSECT",VERTEX,{"derivedFrom":[subQ0,sQuery(id+"F0.wireOp",EDGE,"E9")]}),-1.0]])],"derivedFrom":subQ0})])],"isStart":false});}
            var Q10;
            {var subQ0=sQuery(id+"F0.wireOp",EDGE,"E9");Q10=makeQuery(id+"F1.opExtrude","CAP_EDGE",EDGE,{"disambiguationData":[OSD([subQ0]),TDD([makeQuery(id+"F0.imprint","IMPRINT",EDGE,{"disambiguationData":[TD([[makeQuery(id+"F0.imprint","INTERSECT",VERTEX,{"derivedFrom":[sQuery(id+"F0.wireOp",EDGE,"E2"),subQ0]}),1.0]])],"derivedFrom":subQ0})])],"isStart":false});}
            var Q11;
            {var subQ0=sQuery(id+"F0.wireOp",EDGE,"E12");Q11=makeQuery(id+"F1.opExtrude","CAP_EDGE",EDGE,{"disambiguationData":[OSD([subQ0]),TDD([makeQuery(id+"F0.imprint","IMPRINT",EDGE,{"disambiguationData":[TD([[makeQuery(id+"F0.imprint","INTERSECT",VERTEX,{"derivedFrom":[sQuery(id+"F0.wireOp",EDGE,"E4"),subQ0]}),-1.0]])],"derivedFrom":subQ0})])],"isStart":false});}
            var Q12;
            {var subQ0=sQuery(id+"F0.wireOp",EDGE,"E4");Q12=makeQuery(id+"F1.opExtrude","CAP_EDGE",EDGE,{"disambiguationData":[OSD([subQ0]),TDD([makeQuery(id+"F0.imprint","IMPRINT",EDGE,{"disambiguationData":[TD([[makeQuery(id+"F0.imprint","INTERSECT",VERTEX,{"derivedFrom":[subQ0,sQuery(id+"F0.wireOp",EDGE,"E9")]}),-1.0]])],"derivedFrom":subQ0})])],"isStart":false});}
            var Q13;
            {var subQ0=sQuery(id+"F0.wireOp",EDGE,"E9");Q13=makeQuery(id+"F1.opExtrude","CAP_EDGE",EDGE,{"disambiguationData":[OSD([subQ0]),TDD([makeQuery(id+"F0.imprint","IMPRINT",EDGE,{"disambiguationData":[TD([[makeQuery(id+"F0.imprint","INTERSECT",VERTEX,{"derivedFrom":[sQuery(id+"F0.wireOp",EDGE,"E4"),subQ0]}),1.0]])],"derivedFrom":subQ0})])],"isStart":false});}
            var Q14;
            {var subQ0=sQuery(id+"F0.wireOp",EDGE,"E14");Q14=makeQuery(id+"F1.opExtrude","CAP_EDGE",EDGE,{"disambiguationData":[OSD([subQ0]),TDD([makeQuery(id+"F0.imprint","IMPRINT",EDGE,{"disambiguationData":[TD([[makeQuery(id+"F0.imprint","INTERSECT",VERTEX,{"derivedFrom":[sQuery(id+"F0.wireOp",EDGE,"E4"),subQ0]}),-1.0]])],"derivedFrom":subQ0})])],"isStart":false});}
            var Q15;
            {var subQ0=sQuery(id+"F0.wireOp",EDGE,"E6");Q15=makeQuery(id+"F1.opExtrude","CAP_EDGE",EDGE,{"disambiguationData":[OSD([subQ0]),TDD([makeQuery(id+"F0.imprint","IMPRINT",EDGE,{"disambiguationData":[TD([[makeQuery(id+"F0.imprint","INTERSECT",VERTEX,{"derivedFrom":[sQuery(id+"F0.wireOp",EDGE,"E4"),subQ0]}),1.0]])],"derivedFrom":subQ0})])],"isStart":false});}
            var Q16;
            {var subQ0=sQuery(id+"F0.wireOp",EDGE,"E14");Q16=makeQuery(id+"F1.opExtrude","CAP_EDGE",EDGE,{"disambiguationData":[OSD([subQ0]),TDD([makeQuery(id+"F0.imprint","IMPRINT",EDGE,{"disambiguationData":[TD([[makeQuery(id+"F0.imprint","INTERSECT",VERTEX,{"derivedFrom":[sQuery(id+"F0.wireOp",EDGE,"E1"),subQ0]}),-1.0]])],"derivedFrom":subQ0})])],"isStart":false});}
            var Q17;
            {var subQ0=sQuery(id+"F0.wireOp",EDGE,"E1");Q17=makeQuery(id+"F1.opExtrude","CAP_EDGE",EDGE,{"disambiguationData":[OSD([subQ0]),TDD([makeQuery(id+"F0.imprint","IMPRINT",EDGE,{"disambiguationData":[TD([[makeQuery(id+"F0.imprint","INTERSECT",VERTEX,{"derivedFrom":[subQ0,sQuery(id+"F0.wireOp",EDGE,"E6")]}),-1.0]])],"derivedFrom":subQ0})])],"isStart":false});}
            var Q18;
            {var subQ0=sQuery(id+"F0.wireOp",EDGE,"E6");Q18=makeQuery(id+"F1.opExtrude","CAP_EDGE",EDGE,{"disambiguationData":[OSD([subQ0]),TDD([makeQuery(id+"F0.imprint","IMPRINT",EDGE,{"disambiguationData":[TD([[makeQuery(id+"F0.imprint","INTERSECT",VERTEX,{"derivedFrom":[sQuery(id+"F0.wireOp",EDGE,"E1"),subQ0]}),1.0]])],"derivedFrom":subQ0})])],"isStart":false});}
            var Q19;
            {var subQ0=sQuery(id+"F0.wireOp",EDGE,"E11");Q19=makeQuery(id+"F1.opExtrude","CAP_EDGE",EDGE,{"disambiguationData":[OSD([subQ0]),TDD([makeQuery(id+"F0.imprint","IMPRINT",EDGE,{"disambiguationData":[TD([[makeQuery(id+"F0.imprint","INTERSECT",VERTEX,{"derivedFrom":[sQuery(id+"F0.wireOp",EDGE,"E1"),subQ0]}),-1.0]])],"derivedFrom":subQ0})])],"isStart":false});}
            var Q20;
            {var subQ0=sQuery(id+"F0.wireOp",EDGE,"E11");Q20=makeQuery(id+"F1.opExtrude","CAP_EDGE",EDGE,{"disambiguationData":[OSD([subQ0]),TDD([makeQuery(id+"F0.imprint","IMPRINT",EDGE,{"disambiguationData":[TD([[makeQuery(id+"F0.imprint","INTERSECT",VERTEX,{"derivedFrom":[sQuery(id+"F0.wireOp",EDGE,"E3"),subQ0]}),-1.0]])],"derivedFrom":subQ0})])],"isStart":false});}
            var Q21;
            {var subQ0=sQuery(id+"F0.wireOp",EDGE,"E1");Q21=makeQuery(id+"F1.opExtrude","CAP_EDGE",EDGE,{"disambiguationData":[OSD([subQ0]),TDD([makeQuery(id+"F0.imprint","IMPRINT",EDGE,{"disambiguationData":[TD([[makeQuery(id+"F0.imprint","INTERSECT",VERTEX,{"derivedFrom":[subQ0,sQuery(id+"F0.wireOp",EDGE,"E8")]}),-1.0]])],"derivedFrom":subQ0})])],"isStart":false});}
            var Q22;
            {var subQ0=sQuery(id+"F0.wireOp",EDGE,"E8");Q22=makeQuery(id+"F1.opExtrude","CAP_EDGE",EDGE,{"disambiguationData":[OSD([subQ0]),TDD([makeQuery(id+"F0.imprint","IMPRINT",EDGE,{"disambiguationData":[TD([[makeQuery(id+"F0.imprint","INTERSECT",VERTEX,{"derivedFrom":[sQuery(id+"F0.wireOp",EDGE,"E1"),subQ0]}),1.0]])],"derivedFrom":subQ0})])],"isStart":false});}
            var Q23;
            {var subQ0=sQuery(id+"F0.wireOp",EDGE,"E3");Q23=makeQuery(id+"F1.opExtrude","CAP_EDGE",EDGE,{"disambiguationData":[OSD([subQ0]),TDD([makeQuery(id+"F0.imprint","IMPRINT",EDGE,{"disambiguationData":[TD([[makeQuery(id+"F0.imprint","INTERSECT",VERTEX,{"derivedFrom":[subQ0,sQuery(id+"F0.wireOp",EDGE,"E8")]}),-1.0]])],"derivedFrom":subQ0})])],"isStart":false});}
            var Q24;
            {var subQ0=sQuery(id+"F0.wireOp",EDGE,"E8");Q24=makeQuery(id+"F1.opExtrude","CAP_EDGE",EDGE,{"disambiguationData":[OSD([subQ0]),TDD([makeQuery(id+"F0.imprint","IMPRINT",EDGE,{"disambiguationData":[TD([[makeQuery(id+"F0.imprint","INTERSECT",VERTEX,{"derivedFrom":[sQuery(id+"F0.wireOp",EDGE,"E3"),subQ0]}),1.0]])],"derivedFrom":subQ0})])],"isStart":false});}
            var Q25;
            {var subQ0=sQuery(id+"F0.wireOp",EDGE,"E13");Q25=makeQuery(id+"F1.opExtrude","CAP_EDGE",EDGE,{"disambiguationData":[OSD([subQ0]),TDD([makeQuery(id+"F0.imprint","IMPRINT",EDGE,{"disambiguationData":[TD([[makeQuery(id+"F0.imprint","INTERSECT",VERTEX,{"derivedFrom":[sQuery(id+"F0.wireOp",EDGE,"E3"),subQ0]}),-1.0]])],"derivedFrom":subQ0})])],"isStart":false});}
            var Q26;
            {var subQ0=sQuery(id+"F0.wireOp",EDGE,"E3");Q26=makeQuery(id+"F1.opExtrude","CAP_EDGE",EDGE,{"disambiguationData":[OSD([subQ0]),TDD([makeQuery(id+"F0.imprint","IMPRINT",EDGE,{"disambiguationData":[TD([[makeQuery(id+"F0.imprint","INTERSECT",VERTEX,{"derivedFrom":[subQ0,sQuery(id+"F0.wireOp",EDGE,"E5")]}),-1.0]])],"derivedFrom":subQ0})])],"isStart":false});}
            var Q27;
            {var subQ0=sQuery(id+"F0.wireOp",EDGE,"E5");Q27=makeQuery(id+"F1.opExtrude","CAP_EDGE",EDGE,{"disambiguationData":[OSD([subQ0]),TDD([makeQuery(id+"F0.imprint","IMPRINT",EDGE,{"disambiguationData":[TD([[makeQuery(id+"F0.imprint","INTERSECT",VERTEX,{"derivedFrom":[sQuery(id+"F0.wireOp",EDGE,"E3"),subQ0]}),1.0]])],"derivedFrom":subQ0})])],"isStart":false});}
            var Q28;
            {var subQ0=sQuery(id+"F0.wireOp",EDGE,"E13");Q28=makeQuery(id+"F1.opExtrude","CAP_EDGE",EDGE,{"disambiguationData":[OSD([subQ0]),TDD([makeQuery(id+"F0.imprint","IMPRINT",EDGE,{"disambiguationData":[TD([[makeQuery(id+"F0.imprint","INTERSECT",VERTEX,{"derivedFrom":[sQuery(id+"F0.wireOp",EDGE,"E0"),subQ0]}),-1.0]])],"derivedFrom":subQ0})])],"isStart":false});}
            var Q29;
            {var subQ0=sQuery(id+"F0.wireOp",EDGE,"E4");Q29=makeQuery(id+"F1.opExtrude","CAP_EDGE",EDGE,{"disambiguationData":[OSD([subQ0]),TDD([makeQuery(id+"F0.imprint","IMPRINT",EDGE,{"disambiguationData":[TD([[makeQuery(id+"F0.imprint","INTERSECT",VERTEX,{"derivedFrom":[subQ0,sQuery(id+"F0.wireOp",EDGE,"E6")]}),-1.0]])],"derivedFrom":subQ0})])],"isStart":false});}
            fillet(context, id + "F2", {"entities" : qUnion([Q0, Q1, Q2, Q3, Q4, Q5, Q6, Q7, Q8, Q9, Q10, Q11, Q12, Q13, Q14, Q15, Q16, Q17, Q18, Q19, Q20, Q21, Q22, Q23, Q24, Q25, Q26, Q27, Q28, Q29]), "radius" : 5.08 * mm, "tangentPropagation" : true, "allowEdgeOverflow" : false});
        }
    });
